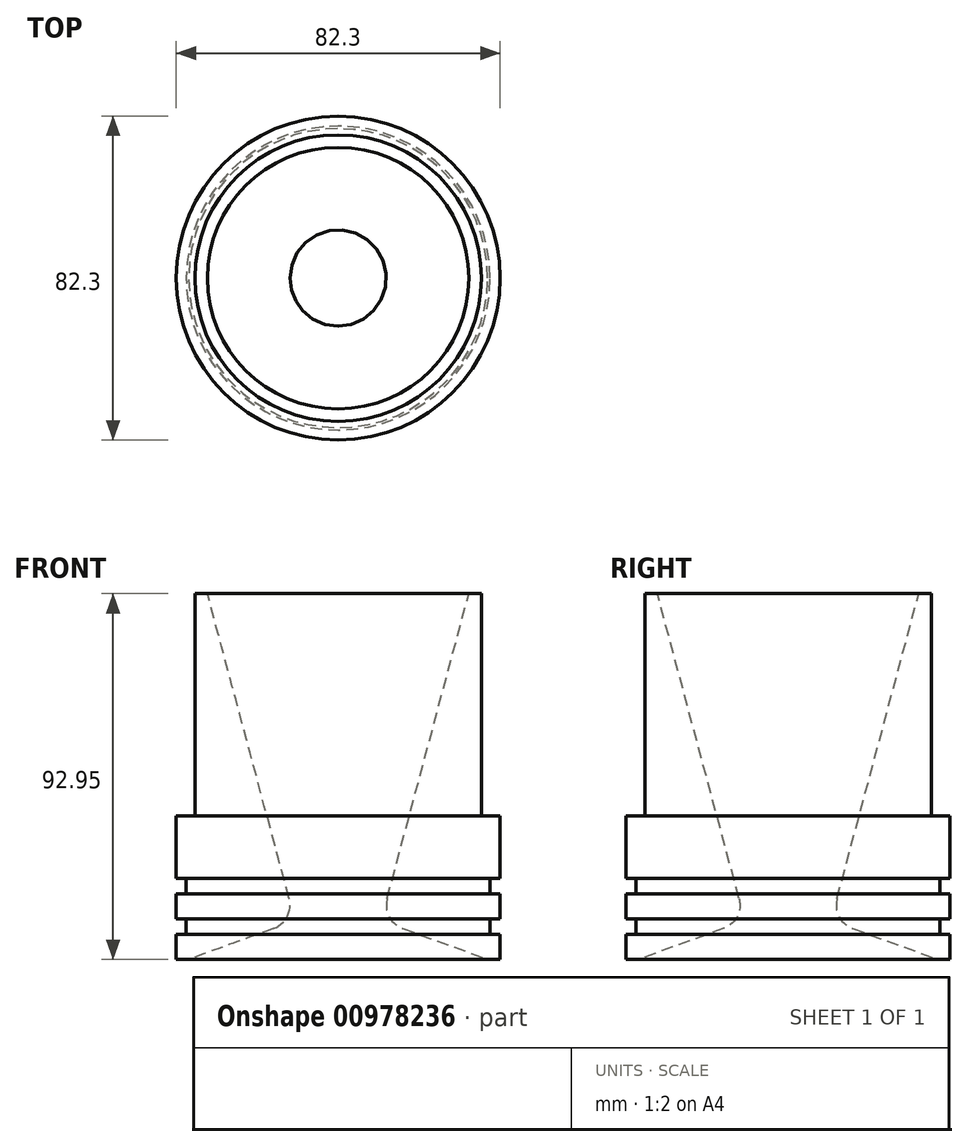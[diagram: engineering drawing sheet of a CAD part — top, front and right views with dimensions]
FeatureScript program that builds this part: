
annotation { "Feature Type Name" : "Feature", "Feature Type Description" : "" }
export const myFeature = defineFeature(function(context is Context, id is Id, definition is map)
    precondition{}
    {
        {
            var Q0;
            Q0=qCreatedBy(makeId("Right.planeOp"),FACE);
            var sketch = newSketch(context, id + "F0", { "sketchPlane" : qUnion([Q0])});
            skLineSegment(sketch, "E0", {"start": v(-12.45, 15.46) * mm, "end": v(-33.21, 92.95) * mm});
            skLineSegment(sketch, "E1", {"start": v(-33.21, 92.95) * mm, "end": v(0, 92.95) * mm, "construction": true});
            skLineSegment(sketch, "E2", {"start": v(-41.15, 6.35) * mm, "end": v(-38.6, 6.35) * mm});
            skLineSegment(sketch, "E3", {"start": v(-38.6, 6.35) * mm, "end": v(-38.6, 10.29) * mm});
            skLineSegment(sketch, "E4", {"start": v(-38.6, 10.29) * mm, "end": v(-41.15, 10.29) * mm});
            skLineSegment(sketch, "E5", {"start": v(-41.15, 10.29) * mm, "end": v(-41.15, 16.64) * mm});
            skLineSegment(sketch, "E6", {"start": v(-41.15, 16.64) * mm, "end": v(-38.6, 16.64) * mm});
            skLineSegment(sketch, "E7", {"start": v(-38.6, 16.64) * mm, "end": v(-38.6, 20.57) * mm});
            skLineSegment(sketch, "E8", {"start": v(-38.6, 20.57) * mm, "end": v(-41.15, 20.57) * mm});
            skLineSegment(sketch, "E9", {"start": v(-41.15, 20.57) * mm, "end": v(-41.15, 36.45) * mm});
            skLineSegment(sketch, "E10", {"start": v(-36.39, 92.95) * mm, "end": v(-33.21, 92.95) * mm});
            skLineSegment(sketch, "E11", {"start": v(0, 0) * mm, "end": v(0, 92.95) * mm, "construction": true});
            skLineSegment(sketch, "E12", {"start": v(-41.15, 6.35) * mm, "end": v(-41.15, 0) * mm});
            skLineSegment(sketch, "E13", {"start": v(-37.97, 0) * mm, "end": v(-16.4, 7.85) * mm});
            skLineSegment(sketch, "E14", {"start": v(-37.97, 0) * mm, "end": v(-41.15, 0) * mm});
            skLineSegment(sketch, "E15", {"start": v(-41.15, 36.45) * mm, "end": v(-36.39, 36.45) * mm});
            skLineSegment(sketch, "E16", {"start": v(-36.39, 36.45) * mm, "end": v(-36.39, 92.95) * mm});
            skArc(sketch, "E17.filletArc", {"start": v(-16.4, 7.85) * mm, "mid": v(-12.95, 10.88) * mm, "end": v(-12.45, 15.46) * mm});
            skSolve(sketch);
        }
        {
            var Q0;
            Q0 = qSketchRegion(id + "F0", true);
            var Q1;
            Q1=sQuery(id+"F0.wireOp",EDGE,"E11");
            revolve(context, id + "F1", {"surfaceOperationType" : NewSurfaceOperationType.NEW, "entities" : qUnion([Q0]), "axis" : qUnion([Q1]), "revolveType" : RevolveType.FULL});
        }
    });
